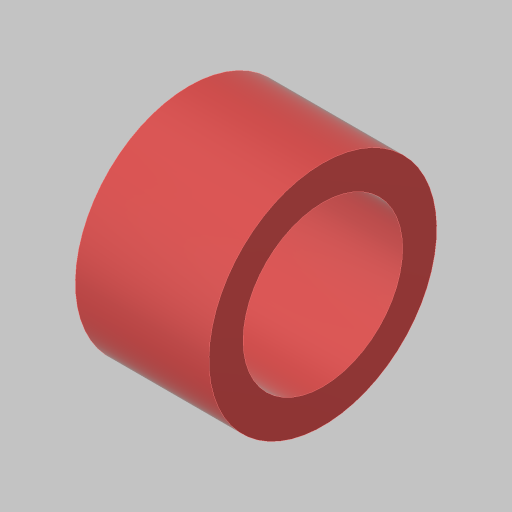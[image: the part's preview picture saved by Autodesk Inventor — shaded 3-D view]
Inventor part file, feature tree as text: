
AUTODESK INVENTOR PART (.ipt)
format: ipt  version: 2023.5 (Build 275446000, 446)  size: 111,104 bytes
history: native  units: in
note: dims shown in document units (in); Inventor stores cm internally (conversion verified against a paired STEP export)
features: extrude x1, sketch x1
ambient origin geometry x8: Origin, YZ Plane, XZ Plane, XY Plane, X Axis, Y Axis, Z Axis, Center Point
bodies: Solid1 (feature_tree)
feature tree (2):
  extrude  "Extrusion1"  Depth=0.49in
  sketch  "Sketch1"  dims[d0=0.585in d1=0.125in d2=0.49in d3=0.0in]
